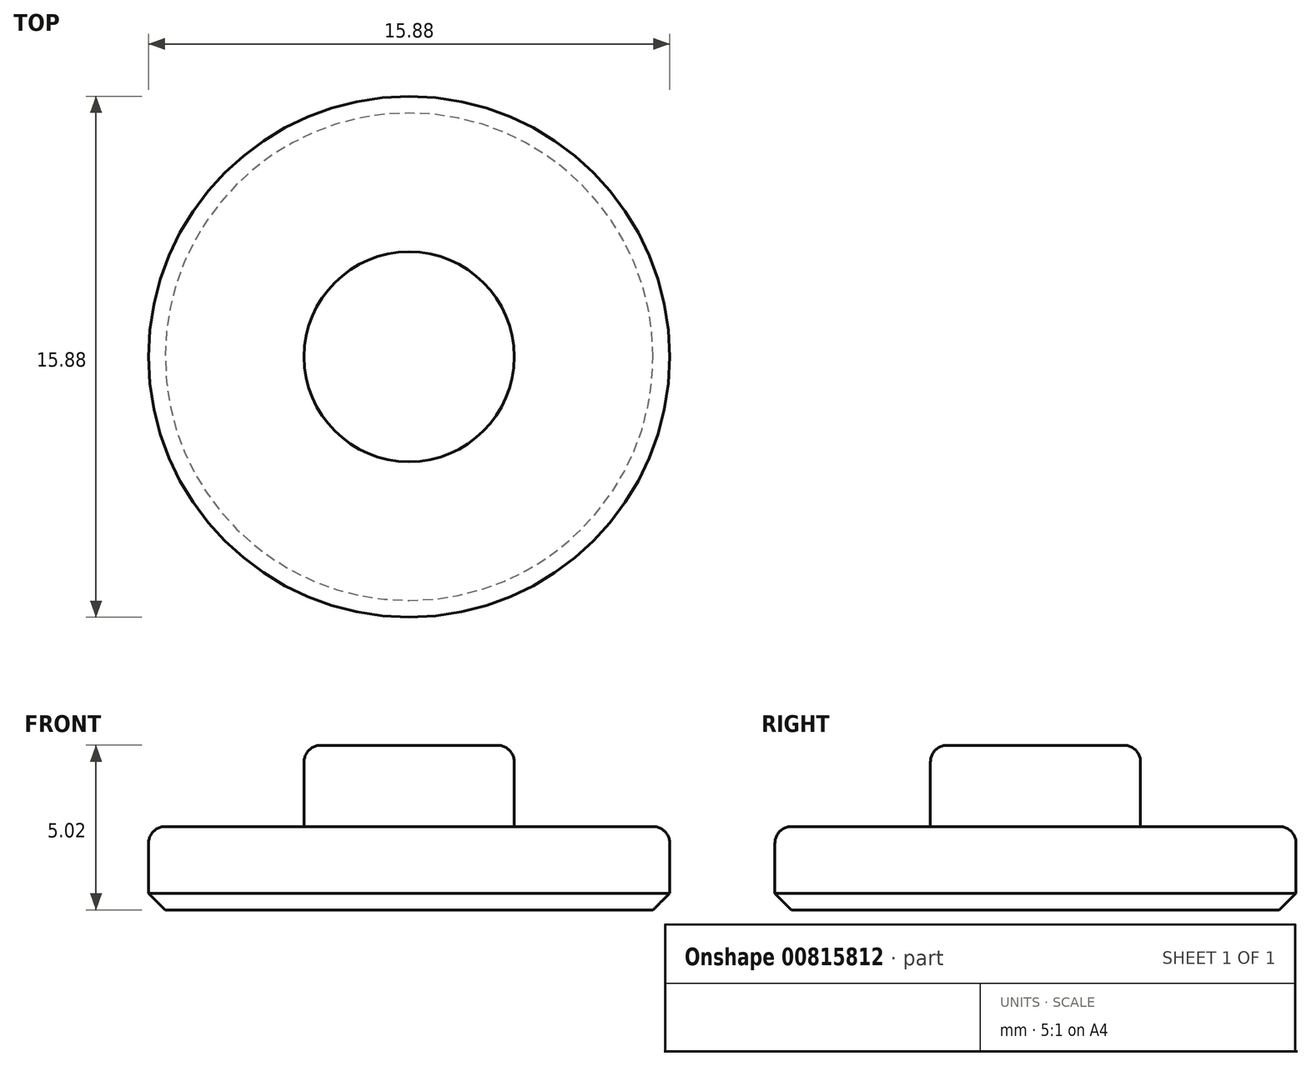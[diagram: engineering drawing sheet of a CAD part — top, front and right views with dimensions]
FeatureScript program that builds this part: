
annotation { "Feature Type Name" : "Feature", "Feature Type Description" : "" }
export const myFeature = defineFeature(function(context is Context, id is Id, definition is map)
    precondition{}
    {
        {
            var Q0;
            Q0=qCreatedBy(makeId("Top.planeOp"),FACE);
            var sketch = newSketch(context, id + "F0", { "sketchPlane" : qUnion([Q0])});
            skCircle(sketch, "E0", {"center": v(0, 0) * mm, "radius": 7.94 * mm});
            skSolve(sketch);
        }
        {
            var Q0;
            Q0=qCreatedBy(makeId("Top.planeOp"),FACE);
            var sketch = newSketch(context, id + "F1", { "sketchPlane" : qUnion([Q0])});
            skCircle(sketch, "E1", {"center": v(0, 0) * mm, "radius": 3.2 * mm});
            skSolve(sketch);
        }
        {
            var Q0;
            Q0 = qSketchRegion(id + "F0", true);
            extrude(context, id + "F2", {"entities" : qUnion([Q0]), "depth" : 2.54 * mm, "offsetDistance" : 25.4 * mm});
        }
        {
            var Q0;
            Q0 = qSketchRegion(id + "F1", true);
            extrude(context, id + "F3", {"entities" : qUnion([Q0]), "operationType" : NewBodyOperationType.ADD, "depth" : 5.02 * mm, "offsetDistance" : 25.4 * mm, "hasSecondDirection" : true, "secondDirectionOppositeDirection" : false, "secondDirectionDepth" : 2.54 * mm});
        }
        {
            var Q0;
            Q0=makeQuery(id+"F3.opExtrude","CAP_FACE",FACE,{"disambiguationData":[OSD([sQuery(id+"F1.wireOp",EDGE,"E1")])],"isStart":false});
            var Q1;
            Q1=makeQuery(id+"F2.opExtrude","CAP_EDGE",EDGE,{"disambiguationData":[OSD([sQuery(id+"F0.wireOp",EDGE,"E0")])],"isStart":false});
            fillet(context, id + "F4", {"entities" : qUnion([Q0, Q1]), "radius" : 0.5 * mm, "tangentPropagation" : true, "allowEdgeOverflow" : false});
        }
        {
            var Q0;
            Q0=makeQuery(id+"F2.opExtrude","CAP_EDGE",EDGE,{"disambiguationData":[OSD([sQuery(id+"F0.wireOp",EDGE,"E0")])],"isStart":true});
            chamfer(context, id + "F5", {"entities" : qUnion([Q0]), "width" : 0.5 * mm, "tangentPropagation" : true});
        }
    });
